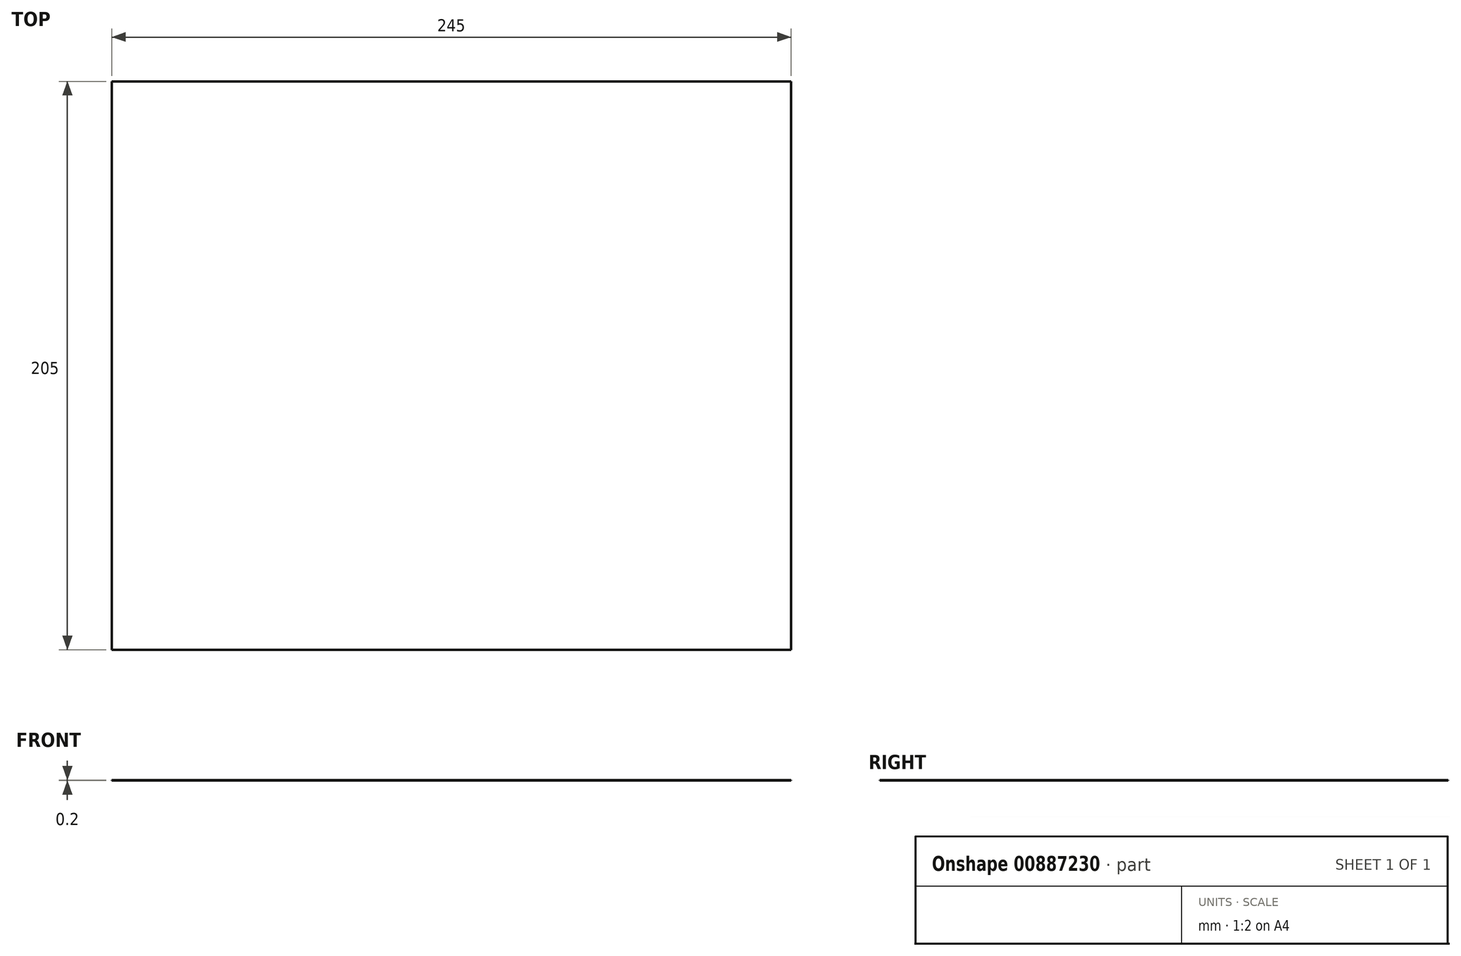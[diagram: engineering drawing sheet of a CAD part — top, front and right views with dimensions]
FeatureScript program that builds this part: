
annotation { "Feature Type Name" : "Feature", "Feature Type Description" : "" }
export const myFeature = defineFeature(function(context is Context, id is Id, definition is map)
    precondition{}
    {
        {
            var Q0;
            Q0=qCreatedBy(makeId("Top.planeOp"), FACE);
            var sketch = newSketch(context, id + "F0", { "sketchPlane" : qUnion([Q0])});
            skLineSegment(sketch, "E0.bottom", {"start": v(0, 0) * mm, "end": v(245, 0) * mm});
            skLineSegment(sketch, "E0.top", {"start": v(0, 205) * mm, "end": v(245, 205) * mm});
            skLineSegment(sketch, "E0.left", {"start": v(0, 0) * mm, "end": v(0, 205) * mm});
            skLineSegment(sketch, "E0.right", {"start": v(245, 0) * mm, "end": v(245, 205) * mm});
            skSolve(sketch);
        }
        {
            var Q0;
            Q0 = qSketchRegion(id + "F0", true);
            extrude(context, id + "F1", {"entities" : qUnion([Q0]), "domain" : OperationDomain.MODEL, "flatOperationType" : FlatOperationType.REMOVE, "depth" : 0.2 * mm, "offsetDistance" : 25 * mm});
        }
    });
